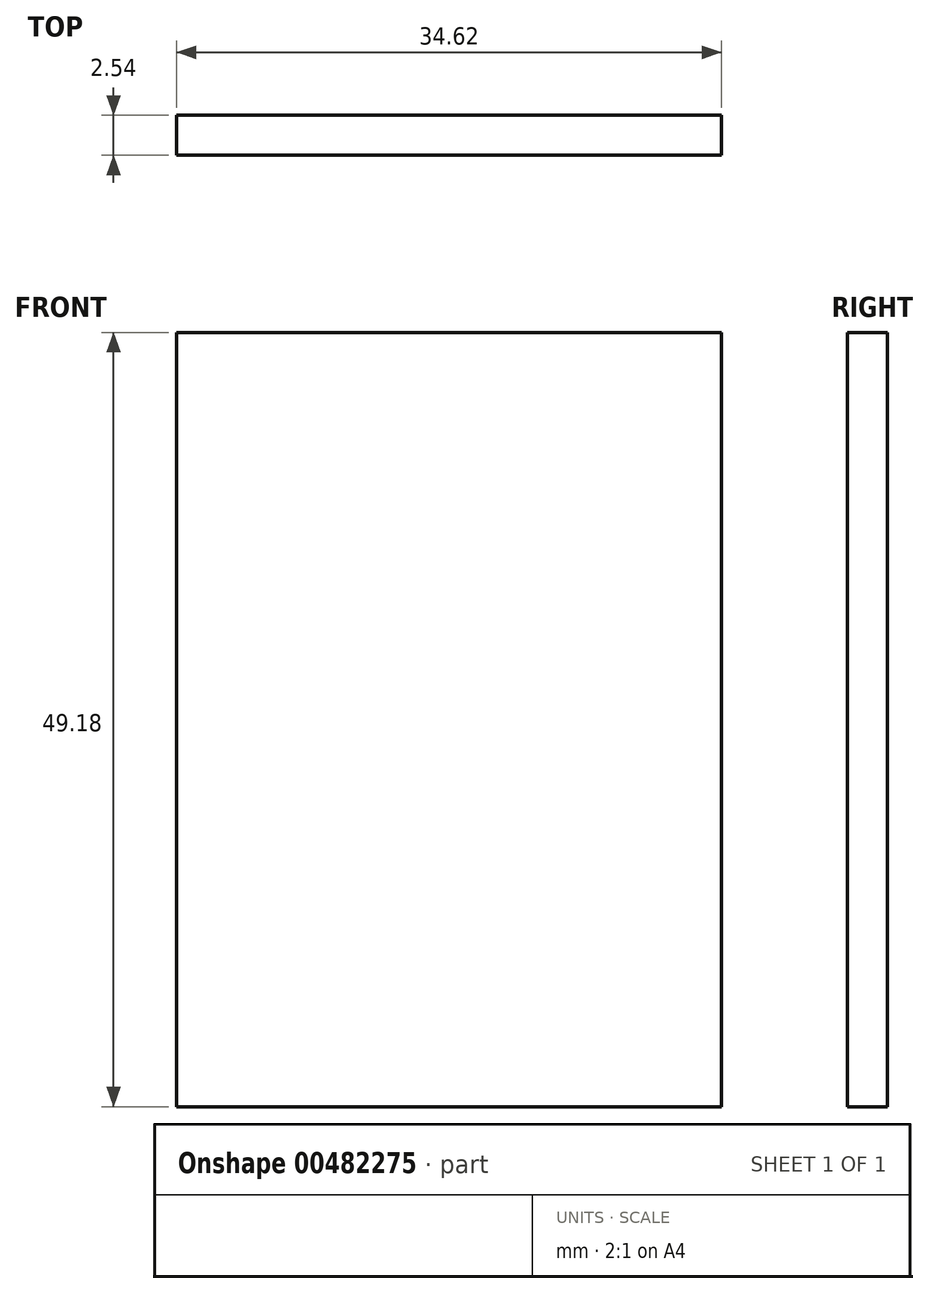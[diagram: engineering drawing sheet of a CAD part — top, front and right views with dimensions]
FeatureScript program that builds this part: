
annotation { "Feature Type Name" : "Feature", "Feature Type Description" : "" }
export const myFeature = defineFeature(function(context is Context, id is Id, definition is map)
    precondition{}
    {
        {
            var Q0;
            Q0=qCreatedBy(makeId("Front.planeOp"),FACE);
            var sketch = newSketch(context, id + "F0", { "sketchPlane" : qUnion([Q0])});
            skLineSegment(sketch, "E0.bottom", {"start": v(17.31, 24.59) * mm, "end": v(-17.31, 24.59) * mm});
            skLineSegment(sketch, "E0.top", {"start": v(17.31, -24.59) * mm, "end": v(-17.31, -24.59) * mm});
            skLineSegment(sketch, "E0.left", {"start": v(17.31, 24.59) * mm, "end": v(17.31, -24.59) * mm});
            skLineSegment(sketch, "E0.right", {"start": v(-17.31, 24.59) * mm, "end": v(-17.31, -24.59) * mm});
            skPoint(sketch, "E0.middle", {"position": v(0, 0) * mm});
            skSolve(sketch);
        }
        {
            var Q0;
            Q0=makeQuery(id+"F0.imprint","IMPRINT",FACE,{"disambiguationData":[TD([[makeQuery(id+"F0.imprint","IMPRINT",EDGE,{"derivedFrom":sQuery(id+"F0.wireOp",EDGE,"E0.bottom")}),1.0]])]});
            extrude(context, id + "F1", {"entities" : qUnion([Q0]), "oppositeDirection" : true, "depth" : 2.54 * mm});
        }
    });
